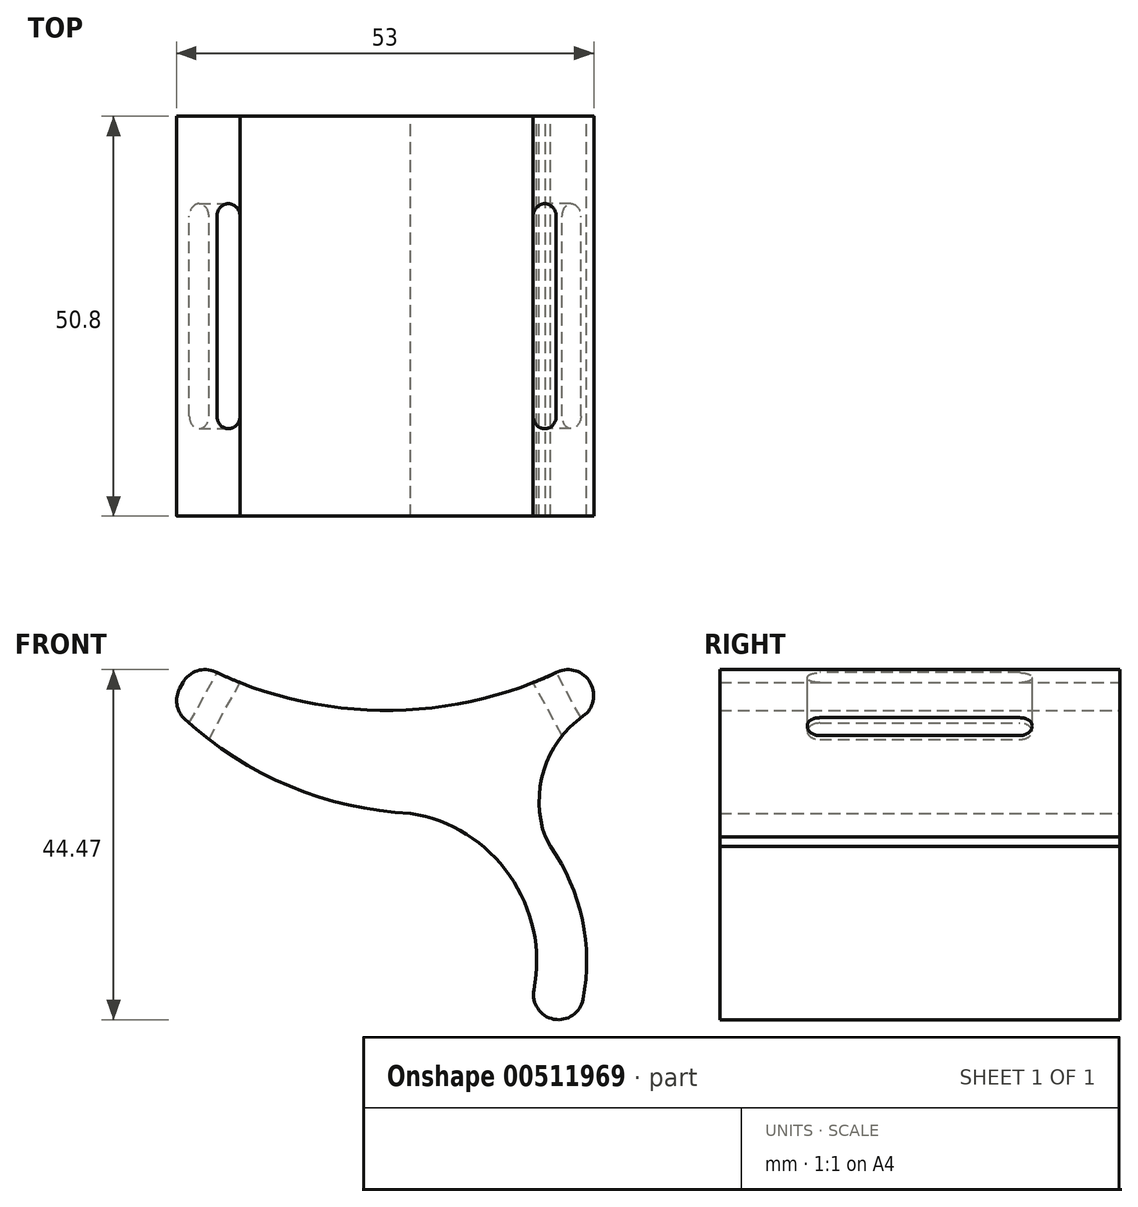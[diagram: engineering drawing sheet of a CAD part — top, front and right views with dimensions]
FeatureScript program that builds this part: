
annotation { "Feature Type Name" : "Feature", "Feature Type Description" : "" }
export const myFeature = defineFeature(function(context is Context, id is Id, definition is map)
    precondition{}
    {
        {
            var Q0;
            Q0=qCreatedBy(makeId("Front.planeOp"),FACE);
            var sketch = newSketch(context, id + "F0", { "sketchPlane" : qUnion([Q0])});
            skArc(sketch, "E0", {"start": v(25.42, -33.08) * mm, "mid": v(24.24, -25.44) * mm, "end": v(20.82, -18.5) * mm});
            skArc(sketch, "E1.0", {"start": v(19.07, -33.08) * mm, "mid": v(14.53, -20.74) * mm, "end": v(3.07, -14.28) * mm});
            skPoint(sketch, "E2.third.point", {"position": v(41.19, -11.1) * mm});
            skPoint(sketch, "E2.third.point.positionSnap0", {"position": v(20.44, -11.1) * mm});
            skPoint(sketch, "E3.third.point", {"position": v(-40.91, -10.8) * mm});
            skPoint(sketch, "E3.third.point.positionSnap0", {"position": v(-20.16, -10.8) * mm});
            skArc(sketch, "E4", {"start": v(-20.41, -18) * mm, "mid": v(-20.27, -17.81) * mm, "end": v(-20.14, -17.63) * mm});
            skPoint(sketch, "E5.first.point", {"position": v(0.02, -14.03) * mm});
            skLineSegment(sketch, "E6", {"start": v(18.01, -39.34) * mm, "end": v(24, -41.43) * mm});
            skArc(sketch, "E7.trimOffspring", {"start": v(24, -41.43) * mm, "mid": v(25.07, -37.31) * mm, "end": v(25.42, -33.08) * mm});
            skArc(sketch, "E8.trimOffspring", {"start": v(18.01, -39.34) * mm, "mid": v(18.8, -36.26) * mm, "end": v(19.07, -33.08) * mm});
            skArc(sketch, "E9", {"start": v(-24.39, 5.03) * mm, "mid": v(0, -1.21) * mm, "end": v(24.38, 5.03) * mm});
            skLineSegment(sketch, "E10", {"start": v(24.38, 5.03) * mm, "end": v(27.43, -0.54) * mm});
            skLineSegment(sketch, "E11", {"start": v(-24.39, 5.03) * mm, "end": v(-27.45, -0.53) * mm});
            skPoint(sketch, "E12.third.point", {"position": v(-6.1, 75.18) * mm});
            skArc(sketch, "E13.trimOffspring", {"start": v(-27.45, -0.53) * mm, "mid": v(-13.5, -10.32) * mm, "end": v(3.07, -14.28) * mm});
            skPoint(sketch, "E14.third.point", {"position": v(42.58, -3.9) * mm});
            skArc(sketch, "E15.trimOffspring", {"start": v(27.43, -0.54) * mm, "mid": v(20.46, -7.47) * mm, "end": v(20.17, -17.3) * mm});
            skLineSegment(sketch, "E16", {"start": v(23.06, 0.84) * mm, "end": v(19.87, 6.65) * mm});
            skLineSegment(sketch, "E17", {"start": v(20.27, -0.69) * mm, "end": v(17.09, 5.12) * mm});
            skLineSegment(sketch, "E18", {"start": v(20.82, -18.5) * mm, "end": v(20.17, -17.3) * mm});
            skLineSegment(sketch, "E19", {"start": v(19.87, 6.65) * mm, "end": v(17.09, 5.12) * mm});
            skLineSegment(sketch, "E20.MirrorCS", {"start": v(-23.06, 0.84) * mm, "end": v(-19.87, 6.65) * mm});
            skLineSegment(sketch, "E21.MirrorCS", {"start": v(-19.87, 6.65) * mm, "end": v(-17.09, 5.12) * mm});
            skLineSegment(sketch, "E22.MirrorCS", {"start": v(-20.27, -0.69) * mm, "end": v(-17.09, 5.12) * mm});
            skPoint(sketch, "E23.endSnap0", {"position": v(-21.46, 3.74) * mm});
            skSolve(sketch);
        }
        {
            var Q0;
            Q0 = qSketchRegion(id + "F0", true);
            extrude(context, id + "F1", {"entities" : qUnion([Q0]), "depth" : 50.8 * mm});
        }
        {
            var Q0;
            Q0=makeQuery(id+"F1.opExtrude","SWEPT_EDGE",EDGE,{"disambiguationData":[OSD([sQuery(id+"F0.wireOp",EDGE,"E6"),sQuery(id+"F0.wireOp",EDGE,"E7.trimOffspring")])]});
            var Q1;
            Q1=makeQuery(id+"F1.opExtrude","SWEPT_EDGE",EDGE,{"disambiguationData":[OSD([sQuery(id+"F0.wireOp",EDGE,"E6"),sQuery(id+"F0.wireOp",EDGE,"E8.trimOffspring")])]});
            fillet(context, id + "F2", {"entities" : qUnion([Q0, Q1]), "radius" : 3.17 * mm, "tangentPropagation" : true, "allowEdgeOverflow" : false});
        }
        {
            var Q0;
            Q0=makeQuery(id+"F1.opExtrude","SWEPT_FACE",FACE,{"disambiguationData":[OSD([sQuery(id+"F0.wireOp",EDGE,"E19")])]});
            var sketch = newSketch(context, id + "F3", { "sketchPlane" : qUnion([Q0])});
            skLineSegment(sketch, "E24", {"start": v(20.62, 0) * mm, "end": v(17.45, 0) * mm});
            skLineSegment(sketch, "E25", {"start": v(17.45, -38.1) * mm, "end": v(17.45, -12.7) * mm});
            skLineSegment(sketch, "E26", {"start": v(20.62, -38.1) * mm, "end": v(20.62, -12.7) * mm});
            skLineSegment(sketch, "E27", {"start": v(20.62, -50.8) * mm, "end": v(17.45, -50.8) * mm});
            skLineSegment(sketch, "E28", {"start": v(17.45, -50.8) * mm, "end": v(17.45, -38.1) * mm});
            skLineSegment(sketch, "E29", {"start": v(20.62, -50.8) * mm, "end": v(20.62, -38.1) * mm});
            skLineSegment(sketch, "E30", {"start": v(20.62, -12.7) * mm, "end": v(20.62, 0) * mm});
            skLineSegment(sketch, "E31", {"start": v(17.45, -12.7) * mm, "end": v(17.45, 0) * mm});
            skArc(sketch, "E32", {"start": v(20.62, -12.7) * mm, "mid": v(19.03, -11.11) * mm, "end": v(17.45, -12.7) * mm});
            skArc(sketch, "E33", {"start": v(17.45, -38.1) * mm, "mid": v(19.03, -39.69) * mm, "end": v(20.62, -38.1) * mm});
            skSolve(sketch);
        }
        {
            var Q0;
            Q0=makeQuery(id+"F3.imprint","IMPRINT",FACE,{"disambiguationData":[TD([[makeQuery(id+"F3.imprint","IMPRINT",EDGE,{"derivedFrom":sQuery(id+"F3.wireOp",EDGE,"E25")}),-1.0]])]});
            extrude(context, id + "F4", {"entities" : qUnion([Q0]), "operationType" : NewBodyOperationType.REMOVE, "oppositeDirection" : true, "depth" : 25.4 * mm, "offsetDistance" : 25.4 * mm});
        }
        {
            var Q0;
            Q0=makeQuery(id+"F1.opExtrude","SWEPT_FACE",FACE,{"disambiguationData":[OSD([sQuery(id+"F0.wireOp",EDGE,"E21.MirrorCS")])]});
            var sketch = newSketch(context, id + "F5", { "sketchPlane" : qUnion([Q0])});
            skLineSegment(sketch, "E34", {"start": v(-17.45, -38.1) * mm, "end": v(-17.45, -12.7) * mm});
            skLineSegment(sketch, "E35", {"start": v(-20.62, -38.1) * mm, "end": v(-20.62, -12.7) * mm});
            skLineSegment(sketch, "E36", {"start": v(-20.62, -38.1) * mm, "end": v(-20.62, -50.8) * mm});
            skLineSegment(sketch, "E37", {"start": v(-20.62, -50.8) * mm, "end": v(-17.45, -50.8) * mm});
            skLineSegment(sketch, "E38", {"start": v(-17.45, -50.8) * mm, "end": v(-17.45, -38.1) * mm});
            skLineSegment(sketch, "E39", {"start": v(-17.45, -12.7) * mm, "end": v(-17.45, 0) * mm});
            skLineSegment(sketch, "E40", {"start": v(-17.45, 0) * mm, "end": v(-20.62, 0) * mm});
            skLineSegment(sketch, "E41", {"start": v(-20.62, 0) * mm, "end": v(-20.62, -12.7) * mm});
            skArc(sketch, "E42", {"start": v(-17.45, -12.7) * mm, "mid": v(-19.03, -11.11) * mm, "end": v(-20.62, -12.7) * mm});
            skArc(sketch, "E43", {"start": v(-20.62, -38.1) * mm, "mid": v(-19.03, -39.69) * mm, "end": v(-17.45, -38.1) * mm});
            skSolve(sketch);
        }
        {
            var Q0;
            Q0=makeQuery(id+"F5.imprint","IMPRINT",FACE,{"disambiguationData":[TD([[makeQuery(id+"F5.imprint","IMPRINT",EDGE,{"derivedFrom":sQuery(id+"F5.wireOp",EDGE,"EpH1RfJW-9XML-lGdX-Of3X-6rrYTCywcIDw")}),1.0]])]});
            var Q1;
            Q1=makeQuery(id+"F5.imprint","IMPRINT",FACE,{"disambiguationData":[TD([[makeQuery(id+"F5.imprint","IMPRINT",EDGE,{"derivedFrom":sQuery(id+"F5.wireOp",EDGE,"E34")}),1.0]])]});
            extrude(context, id + "F6", {"entities" : qUnion([Q0, Q1]), "operationType" : NewBodyOperationType.REMOVE, "oppositeDirection" : true, "depth" : 25.4 * mm, "offsetDistance" : 25.4 * mm});
        }
        {
            var Q0;
            Q0=makeQuery(id+"F1.opExtrude","CAP_FACE",FACE,{"disambiguationData":[OSD([sQuery(id+"F0.wireOp",EDGE,"E0"),sQuery(id+"F0.wireOp",EDGE,"E1.0"),sQuery(id+"F0.wireOp",EDGE,"E6"),sQuery(id+"F0.wireOp",EDGE,"E7.trimOffspring"),sQuery(id+"F0.wireOp",EDGE,"E8.trimOffspring"),sQuery(id+"F0.wireOp",EDGE,"E9"),sQuery(id+"F0.wireOp",EDGE,"E10"),sQuery(id+"F0.wireOp",EDGE,"E11"),sQuery(id+"F0.wireOp",EDGE,"E13.trimOffspring"),sQuery(id+"F0.wireOp",EDGE,"E15.trimOffspring"),sQuery(id+"F0.wireOp",EDGE,"E16"),sQuery(id+"F0.wireOp",EDGE,"E17"),sQuery(id+"F0.wireOp",EDGE,"E18"),sQuery(id+"F0.wireOp",EDGE,"E19")])],"isStart":true});
            var sketch = newSketch(context, id + "F7", { "sketchPlane" : qUnion([Q0])});
            skCircle(sketch, "E44", {"center": v(0, 49.6) * mm, "radius": 50.8 * mm});
            skPoint(sketch, "E44.first.point", {"position": v(24.39, 5.03) * mm});
            skPoint(sketch, "E44.second.point", {"position": v(-24.38, 5.03) * mm});
            skPoint(sketch, "E44.third.point", {"position": v(6.48, 99.98) * mm});
            skSolve(sketch);
        }
        {
            var Q0;
            Q0 = qSketchRegion(id + "F7", true);
            extrude(context, id + "F8", {"entities" : qUnion([Q0]), "operationType" : NewBodyOperationType.REMOVE, "oppositeDirection" : true, "depth" : 50.8 * mm, "offsetDistance" : 25.4 * mm});
        }
        {
            var Q0;
            Q0=makeQuery(id+"F1.opExtrude","SWEPT_EDGE",EDGE,{"disambiguationData":[OSD([sQuery(id+"F0.wireOp",EDGE,"E9"),sQuery(id+"F0.wireOp",EDGE,"E10")])]});
            var Q1;
            Q1=makeQuery(id+"F1.opExtrude","SWEPT_EDGE",EDGE,{"disambiguationData":[OSD([sQuery(id+"F0.wireOp",EDGE,"E10"),sQuery(id+"F0.wireOp",EDGE,"E15.trimOffspring")])]});
            var Q2;
            Q2=makeQuery(id+"F1.opExtrude","SWEPT_EDGE",EDGE,{"disambiguationData":[OSD([sQuery(id+"F0.wireOp",EDGE,"E9"),sQuery(id+"F0.wireOp",EDGE,"E11")])]});
            var Q3;
            Q3=makeQuery(id+"F1.opExtrude","SWEPT_EDGE",EDGE,{"disambiguationData":[OSD([sQuery(id+"F0.wireOp",EDGE,"E11"),sQuery(id+"F0.wireOp",EDGE,"E13.trimOffspring")])]});
            fillet(context, id + "F9", {"entities" : qUnion([Q0, Q1, Q2, Q3]), "radius" : 3.17 * mm, "tangentPropagation" : true, "allowEdgeOverflow" : false});
        }
    });
